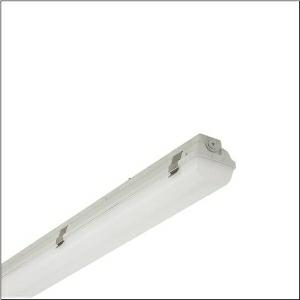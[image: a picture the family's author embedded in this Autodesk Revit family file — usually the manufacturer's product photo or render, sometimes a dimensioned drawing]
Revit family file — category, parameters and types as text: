
# Revit family: monsun_r__21_eco_51fj20dp47a_195a
name_source: partatom
category: Lighting Fixtures
units: mm (PartAtom-declared; Revit-internal decimal feet)

## family parameters
Cut with Voids When Loaded = No
Host = Face
Light Source = No
Part Type = Normal
Room Calculation Point = No
Round Connector Dimension = Use Diameter
Shared = No

## types (1)
- Monsun® 21 Eco (1 x LED, 6600 lm, 50 W, 4000K)
    Apparent Load = 50 VA
    CIE Flux Codes = 40 69 88 88 100
    Color Rendering = 80
    Color Temperature = 4000K
    Default Elevation = 1800 mm
    Description = Monsun® 21 Eco, damp-proof luminaire, primary optical cover: diffuser, of PC, UV-stabilised, frosted, light emission: direct distribution, primary light characteristic: symmetric, installation type: suspended mounting, surface-mounted, LED, rated luminous flux: 6.600lm, luminous efficacy: 132lm/W, light colour: 840, colour temperature: 4000K, control gear: ECG DALI, with terminal, 5-pole, max. 2.5mm², mains connection: 220..240V, AC, 50/60Hz, rated input power: 50W, housing, of glass-fibre reinforced polyester, light grey (RAL 7035), length: 1.577mm, width: 90mm, height: 95mm, clip for enclosure, of spring steel V2A, protection rating (complete): IP66, insulation class (complete): insulation class I (protective earthing), certification: CE, UKCA, protection symbol: D, impact resistance: IK08, permissible operating ambient temperature: -20..+35°C, corresponds to IFS (International Featured Standards) requirements for safety and quality in the food industry, packaging unit: 1 piece
    Height = 103 mm
    Lamp = 1 x LED
    Lamp Light Flux = 6600 lm
    Lamp Power = 50 W
    Lamp count = 1
    Length = 1577 mm
    Luminous efficacy = 132 lm/W
    Manufacturer = Siteco
    ModVariant = No
    Model = 51FJ20DP47A
    Mounting Place = Ceiling
    Mounting Type = Surface mounted
    Number of Poles = 1
    OnlyDefault = Yes
    Power Factor = 1
    Product Name = Monsun® 21 Eco
    Product group = damp-proof luminaire | ceiling mounted
    ProductGroupID = 300
    Protection Class = Protection class I
    Protection Degree = IP 66
    RLX_Detail_Level = 1
    RlxData = <blob elided: 33249 chars, md5=74b8853b>
    Socket = socket
    Standby Power = 0 W
    System Light Flux = 6600 lm
    System Power = 50 W
    Type Comments = Product without accessories
    Type Image = l_1007218.jpg
    URL = http://relux.com
    VarID = ---
    Voltage = 0 V
    Weight = 0.00 kg
    Width = 90 mm

## geometry (parser evidence)
native form markers: Blend x4, Sweep x11
no freeform markers — native parametric forms only
